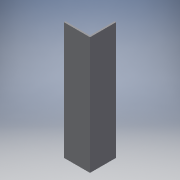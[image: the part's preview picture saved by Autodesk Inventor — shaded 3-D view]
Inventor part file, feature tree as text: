
AUTODESK INVENTOR PART (.ipt)
format: ipt  version: 2017 (Build 210142000, 142)  size: 93,696 bytes
history: native  units: in
note: dims shown in document units (in); Inventor stores cm internally (conversion verified against a paired STEP export)
features: extrude x1, sketch x1
ambient origin geometry x8: Origin, YZ Plane, XZ Plane, XY Plane, X Axis, Y Axis, Z Axis, Center Point
bodies: Solid1 (feature_tree)
feature tree (2):
  extrude  "Extrusion1"  Depth=0.0625in
  sketch  "Sketch1"  dims[d0=1.0in d1=0.0625in d4=1.0in d5=0.0625in d6=4.5in d7=0.0in]
